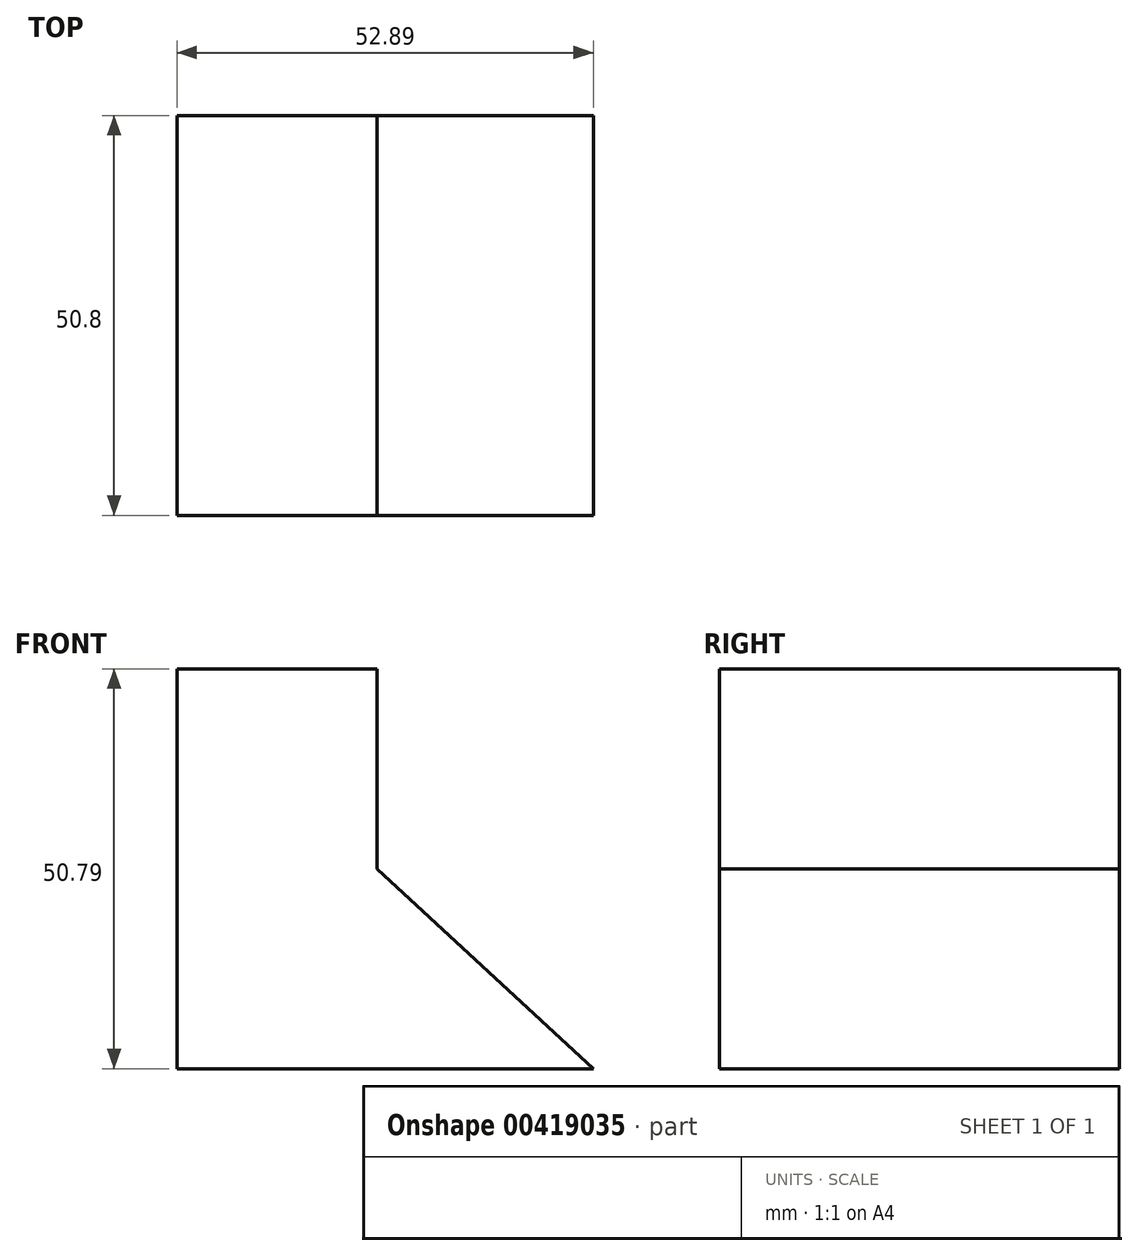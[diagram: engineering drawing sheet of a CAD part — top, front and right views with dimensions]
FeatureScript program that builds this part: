
annotation { "Feature Type Name" : "Feature", "Feature Type Description" : "" }
export const myFeature = defineFeature(function(context is Context, id is Id, definition is map)
    precondition{}
    {
        {
            var Q0;
            Q0=qCreatedBy(makeId("Front.planeOp"),FACE);
            var sketch = newSketch(context, id + "F0", { "sketchPlane" : qUnion([Q0])});
            skLineSegment(sketch, "E0", {"start": v(0, 0) * mm, "end": v(-52.9, 0) * mm});
            skLineSegment(sketch, "E1", {"start": v(-52.9, 0) * mm, "end": v(-52.9, 50.8) * mm});
            skLineSegment(sketch, "E2", {"start": v(-52.9, 50.8) * mm, "end": v(-27.5, 50.8) * mm});
            skLineSegment(sketch, "E3", {"start": v(-27.5, 50.8) * mm, "end": v(-27.5, 25.4) * mm});
            skLineSegment(sketch, "E4", {"start": v(-27.5, 25.4) * mm, "end": v(0, 0) * mm});
            skSolve(sketch);
        }
        {
            var Q0;
            Q0=makeQuery(id+"F0.imprint","IMPRINT",FACE,{"disambiguationData":[TD([[makeQuery(id+"F0.imprint","IMPRINT",EDGE,{"derivedFrom":sQuery(id+"F0.wireOp",EDGE,"E0")}),-1.0]])]});
            extrude(context, id + "F1", {"entities" : qUnion([Q0]), "depth" : 50.8 * mm});
        }
    });
